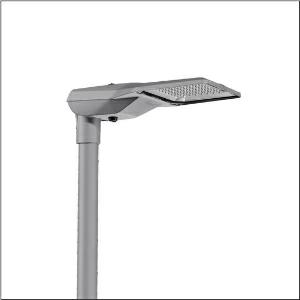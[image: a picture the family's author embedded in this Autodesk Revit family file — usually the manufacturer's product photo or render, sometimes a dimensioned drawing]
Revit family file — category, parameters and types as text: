
# Revit family: streetlight_sl_21_iq_midi___st1_0a_5xe3d61y08nb_32be
name_source: partatom
category: Lighting Fixtures
units: mm (PartAtom-declared; Revit-internal decimal feet)

## family parameters
Cut with Voids When Loaded = No
Host = Face
Light Source = No
Part Type = Normal
Room Calculation Point = No
Round Connector Dimension = Use Diameter
Shared = No

## types (1)
- --- (1 x LED, 18700 lm, 136.6 W, 2700K)
    Apparent Load = 137 VA
    CIE Flux Codes = 40 73 97 100 100
    Color Rendering = 70
    Color Temperature = 2700K
    Default Elevation = 1800 mm
    Description = Streetlight SL 21 iQ midi, mast luminaire, primary light control with lens, of PMMA, primary optical cover: cover, of toughened safety glass, transparent, light distribution: ST1.0a, light emission: direct distribution, primary light characteristic: asymmetric, installation type: post-top, side-entry, LED, High Power LED, rated luminous flux: 18.700lm, luminous efficacy: 137lm/W, light colour: 727, colour temperature: 2700K, control: presetting dimming logarithmic, Street-Remote, Auto-Match, Temp-Guard, Lumen-Switch, Night-Set, Smart-Wire, Light-Fading, Desk-Remote (wireless, voltage-free reading and setting of iQ features in the workshop via application-optimized NFC function/RFID function), optimised constant luminous flux control (CLO 2.0), mains connection: 230..240V, AC, 50/60Hz, start of lifetime: 137W, end of service life: 144W, reduction: 61W, luminaire housing, of diecast aluminium, powder-coated, Siteco® metallic grey (DB 702S), corrosivity category C5 mid according to DIN EN ISO 12944, please order mast flange separately, inclination adjustable: 0°, 5°, 10°, 15°, sealing non-destructively replaceable, multi-level sealing system, length: 644mm, width: 335mm, height: 110mm, mast flange for spigot size: 42mm (side-entry): 5XC10008XM4, 60/48mm (side-entry/post-top): 5XC10108XM2, 76/60mm (side-entry/post-top): 5XC10108XM1, Smart Interface below and above, protection rating (complete): IP66, insulation class (complete): insulation class II (safety insulation), certification: CE, ENEC, ENEC+, VDE, impact resistance: IK09, permissible operating ambient temperature for outdoor applications: -40..+50°C, standard-compliant lighting for roads and squares, packaging unit: 1 piece

Light Distribution: ST1.0a
    Height = 111 mm
    Lamp = 1 x LED
    Lamp Light Flux = 18700 lm
    Lamp Power = 136.6 W
    Lamp count = 1
    Length = 644 mm
    Luminous efficacy = 137 lm/W
    Manufacturer = Siteco
    ModVariant = No
    Model = 5XE3D61Y08NB
    Number of Poles = 1
    OnlyDefault = Yes
    Power Factor = 1
    Product Name = Streetlight SL 21 iQ midi | ST1.0a
    Product group = mast luminaire | pylon top
    ProductGroupID = 6100
    Protection Class = Protection class II
    Protection Degree = IP 66
    RLX_Detail_Level = 1
    RLX_Emergency_Light_Flux = 0 lm
    RLX_Emergency_Type = 0
    RLX_Emergency_Type_DB = No
    RlxData = <blob elided: 91117 chars, md5=52848e66>
    Socket = socket
    Standby Power = 0 W
    System Light Flux = 18701 lm
    System Power = 137 W
    Type Comments = factory setting: luminous flux: 100 % | dim-lin: 254 | 733 mA
    Type Image = l_1004304.jpg
    URL = http://relux.com
    VarID = @adj_043883
    Voltage = 0 V
    Weight = 0.00 kg
    Width = 336 mm

## geometry (parser evidence)
native form markers: Blend x4, Sweep x10
no freeform markers — native parametric forms only
